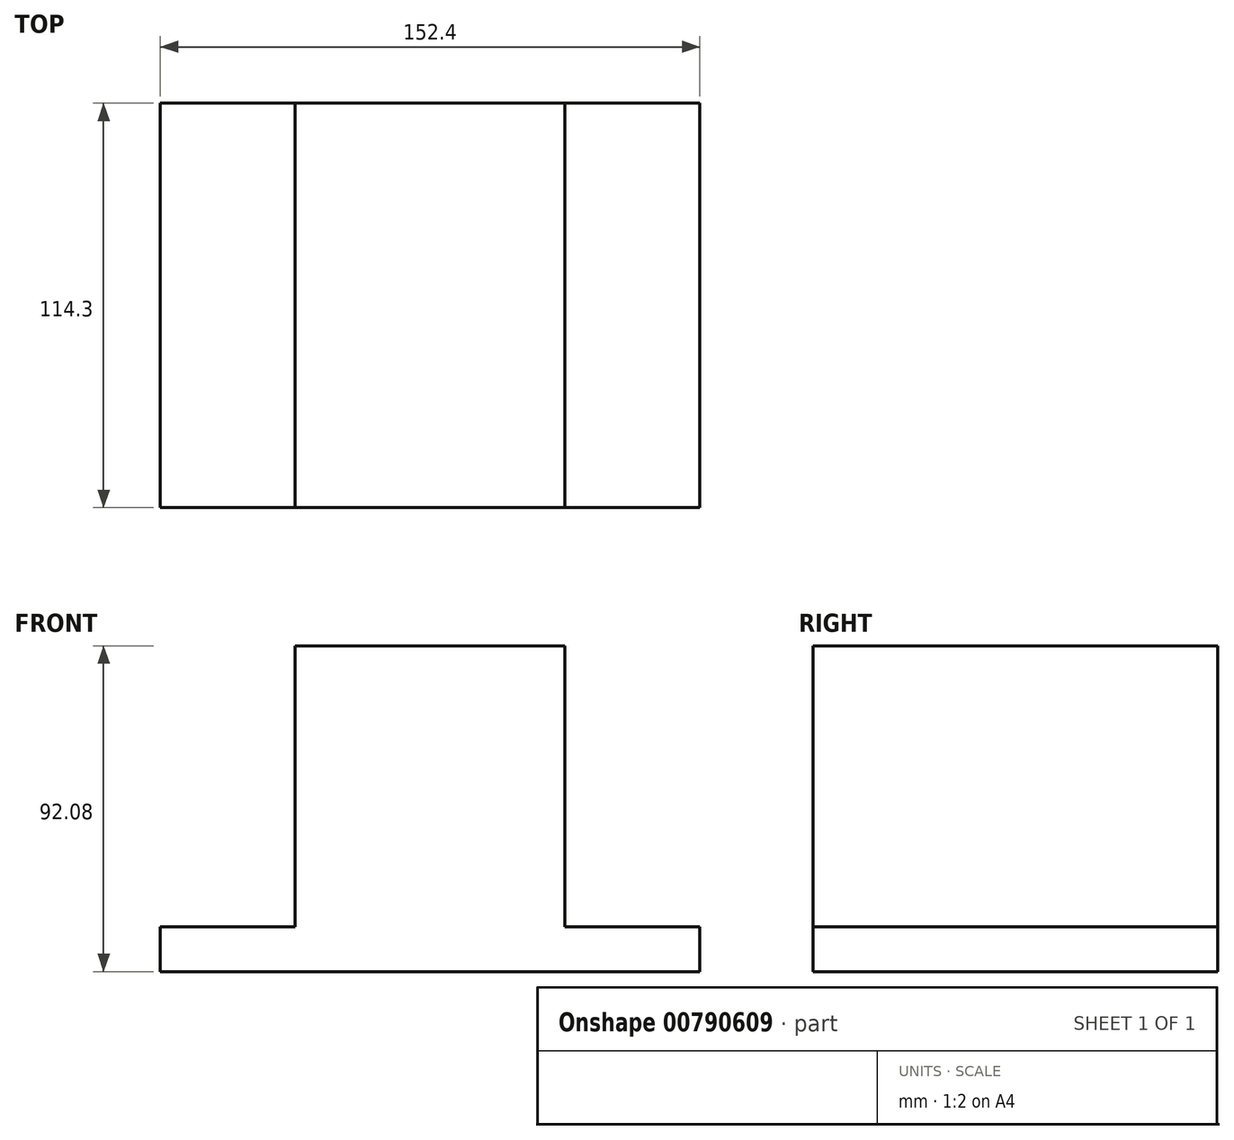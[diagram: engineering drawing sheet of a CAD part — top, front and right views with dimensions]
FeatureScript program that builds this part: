
annotation { "Feature Type Name" : "Feature", "Feature Type Description" : "" }
export const myFeature = defineFeature(function(context is Context, id is Id, definition is map)
    precondition{}
    {
        {
            var Q0;
            Q0=qCreatedBy(makeId("Front.planeOp"),FACE);
            var sketch = newSketch(context, id + "F0", { "sketchPlane" : qUnion([Q0])});
            skLineSegment(sketch, "E0", {"start": v(0, 0) * mm, "end": v(152.4, 0) * mm});
            skLineSegment(sketch, "E1", {"start": v(152.4, 0) * mm, "end": v(152.4, 12.7) * mm});
            skLineSegment(sketch, "E2", {"start": v(152.4, 12.7) * mm, "end": v(114.3, 12.7) * mm});
            skLineSegment(sketch, "E3", {"start": v(114.3, 12.7) * mm, "end": v(114.3, 92.07) * mm});
            skLineSegment(sketch, "E4", {"start": v(114.3, 92.07) * mm, "end": v(38.1, 92.07) * mm});
            skLineSegment(sketch, "E5", {"start": v(38.1, 92.07) * mm, "end": v(38.1, 12.7) * mm});
            skLineSegment(sketch, "E6", {"start": v(38.1, 12.7) * mm, "end": v(0, 12.7) * mm});
            skLineSegment(sketch, "E7", {"start": v(0, 12.7) * mm, "end": v(0, 0) * mm});
            skSolve(sketch);
        }
        {
            var Q0;
            Q0=makeQuery(id+"F0.imprint","IMPRINT",FACE,{"disambiguationData":[TD([[makeQuery(id+"F0.imprint","IMPRINT",EDGE,{"derivedFrom":sQuery(id+"F0.wireOp",EDGE,"E0")}),1.0]])]});
            extrude(context, id + "F1", {"entities" : qUnion([Q0]), "depth" : 114.3 * mm, "offsetDistance" : 25.4 * mm});
        }
    });
